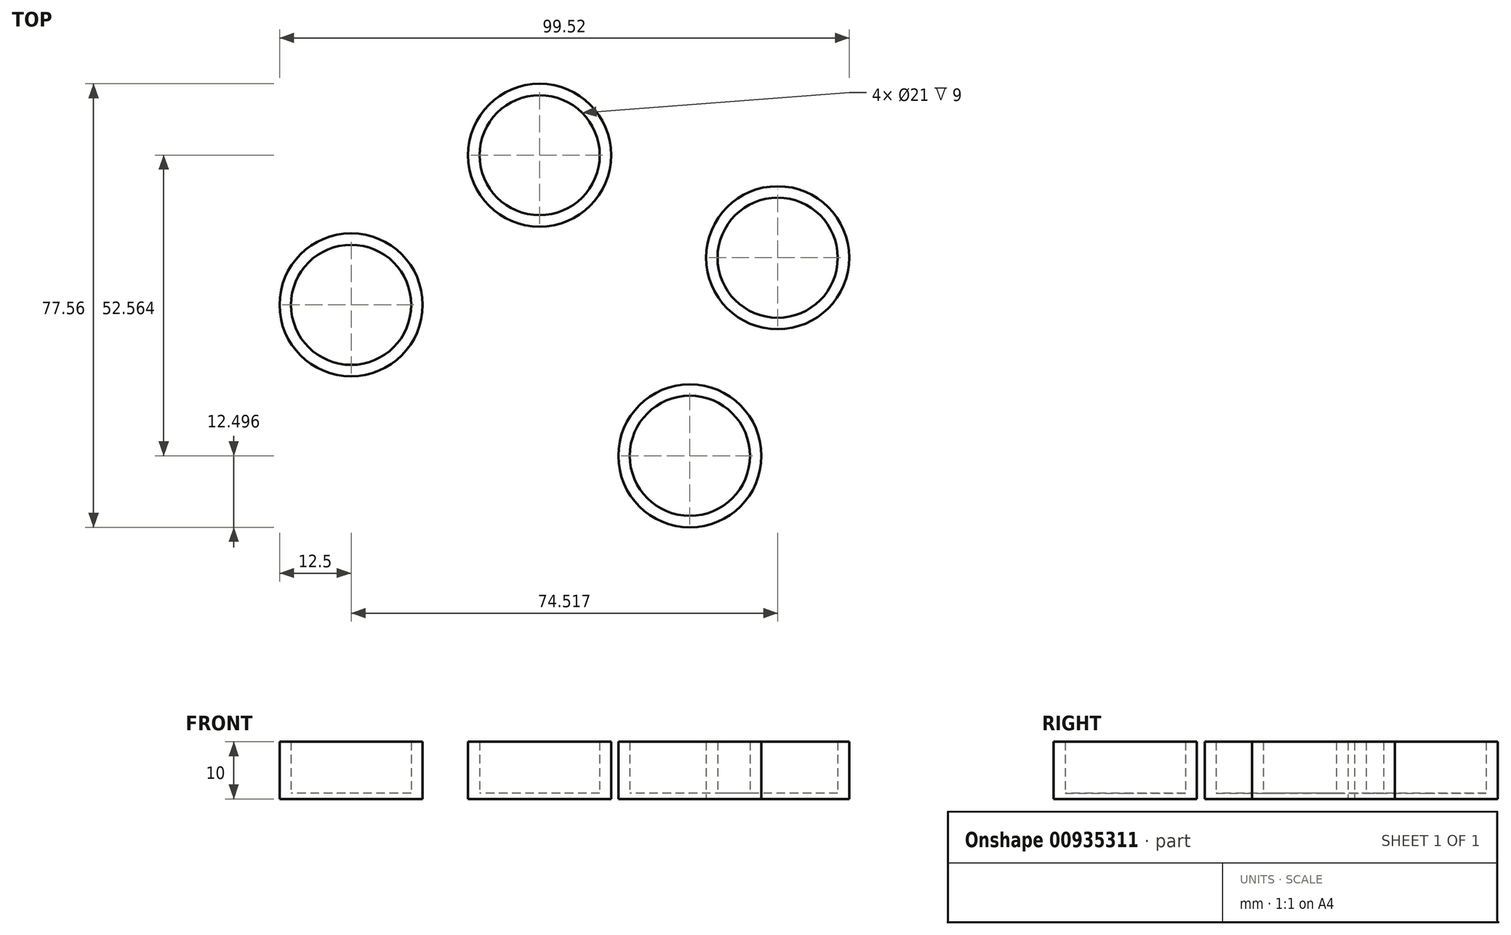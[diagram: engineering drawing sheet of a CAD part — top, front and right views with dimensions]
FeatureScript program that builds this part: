
annotation { "Feature Type Name" : "Feature", "Feature Type Description" : "" }
export const myFeature = defineFeature(function(context is Context, id is Id, definition is map)
    precondition{}
    {
        {
            var Q0;
            Q0=qCreatedBy(makeId("Top.planeOp"),FACE);
            var sketch = newSketch(context, id + "F0", { "sketchPlane" : qUnion([Q0])});
            skCircle(sketch, "E0", {"center": v(-41.02, -28.17) * mm, "radius": 10.5 * mm});
            skCircle(sketch, "E1.0", {"center": v(-41.02, -28.17) * mm, "radius": 12.5 * mm});
            skCircle(sketch, "E2", {"center": v(-8.09, -2) * mm, "radius": 10.5 * mm});
            skCircle(sketch, "E3.0", {"center": v(-8.09, -2) * mm, "radius": 12.5 * mm});
            skCircle(sketch, "E4", {"center": v(33.5, -19.93) * mm, "radius": 10.5 * mm});
            skCircle(sketch, "E5.0", {"center": v(33.5, -19.93) * mm, "radius": 12.5 * mm});
            skCircle(sketch, "E6", {"center": v(18.16, -54.56) * mm, "radius": 10.5 * mm});
            skCircle(sketch, "E7.0", {"center": v(18.16, -54.56) * mm, "radius": 12.5 * mm});
            skSolve(sketch);
        }
        {
            var Q0;
            Q0 = qSketchRegion(id + "F0", true);
            extrude(context, id + "F1", {"entities" : qUnion([Q0]), "depth" : 10 * mm, "offsetDistance" : 25 * mm});
        }
        {
            var Q0;
            Q0=makeQuery(id+"F0.imprint","IMPRINT",FACE,{"disambiguationData":[TD([[makeQuery(id+"F0.imprint","IMPRINT",EDGE,{"derivedFrom":sQuery(id+"F0.wireOp",EDGE,"E0")}),1.0]])]});
            var Q1;
            Q1=makeQuery(id+"F0.imprint","IMPRINT",FACE,{"disambiguationData":[TD([[makeQuery(id+"F0.imprint","IMPRINT",EDGE,{"derivedFrom":sQuery(id+"F0.wireOp",EDGE,"E2")}),1.0]])]});
            var Q2;
            Q2=makeQuery(id+"F0.imprint","IMPRINT",FACE,{"disambiguationData":[TD([[makeQuery(id+"F0.imprint","IMPRINT",EDGE,{"derivedFrom":sQuery(id+"F0.wireOp",EDGE,"E4")}),1.0]])]});
            var Q3;
            Q3=makeQuery(id+"F0.imprint","IMPRINT",FACE,{"disambiguationData":[TD([[makeQuery(id+"F0.imprint","IMPRINT",EDGE,{"derivedFrom":sQuery(id+"F0.wireOp",EDGE,"E6")}),1.0]])]});
            extrude(context, id + "F2", {"entities" : qUnion([Q0, Q1, Q2, Q3]), "operationType" : NewBodyOperationType.ADD, "depth" : 1 * mm, "offsetDistance" : 25 * mm});
        }
    });
